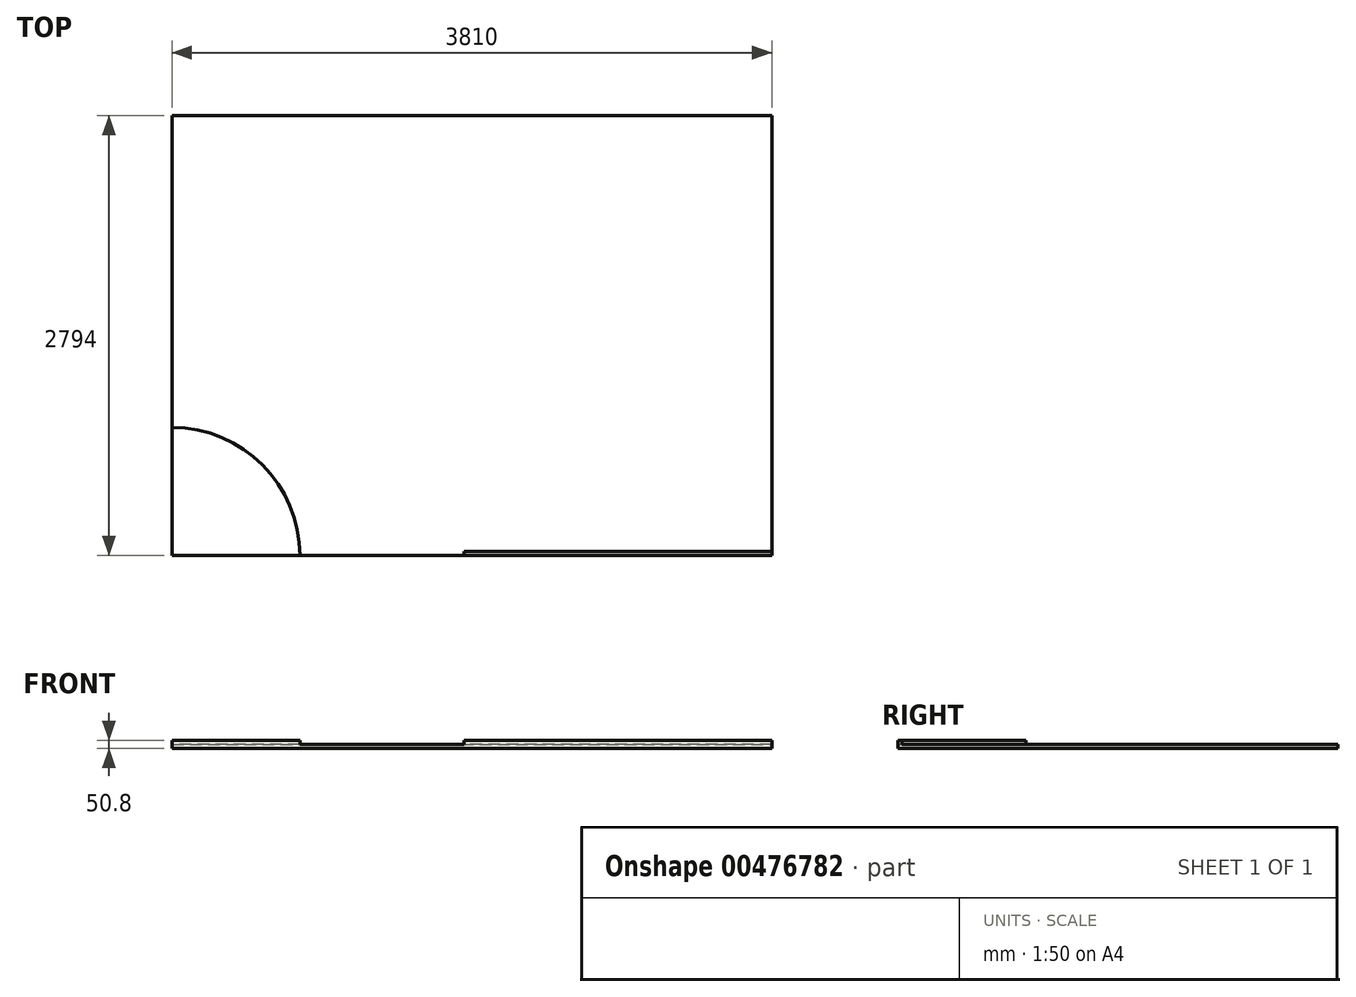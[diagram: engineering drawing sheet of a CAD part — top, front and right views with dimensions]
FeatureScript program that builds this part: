
annotation { "Feature Type Name" : "Feature", "Feature Type Description" : "" }
export const myFeature = defineFeature(function(context is Context, id is Id, definition is map)
    precondition{}
    {
        {
            var Q0;
            Q0=qCreatedBy(makeId("Top.planeOp"),FACE);
            var sketch = newSketch(context, id + "F0", { "sketchPlane" : qUnion([Q0])});
            skLineSegment(sketch, "E0.bottom", {"start": v(0, 0) * mm, "end": v(3810, 0) * mm});
            skLineSegment(sketch, "E0.top", {"start": v(0, 2794) * mm, "end": v(3810, 2794) * mm});
            skLineSegment(sketch, "E0.left", {"start": v(0, 0) * mm, "end": v(0, 2794) * mm});
            skLineSegment(sketch, "E0.right", {"start": v(3810, 0) * mm, "end": v(3810, 2794) * mm});
            skSolve(sketch);
        }
        {
            var Q0;
            Q0 = qSketchRegion(id + "F0", true);
            extrude(context, id + "F1", {"entities" : qUnion([Q0]), "depth" : 25.4 * mm});
        }
        {
            var Q0;
            Q0=makeQuery(id+"F1.opExtrude","CAP_FACE",FACE,{"disambiguationData":[OSD([sQuery(id+"F0.wireOp",EDGE,"E0.bottom"),sQuery(id+"F0.wireOp",EDGE,"E0.top"),sQuery(id+"F0.wireOp",EDGE,"E0.left"),sQuery(id+"F0.wireOp",EDGE,"E0.right")])],"isStart":false});
            var sketch = newSketch(context, id + "F2", { "sketchPlane" : qUnion([Q0])});
            skArc(sketch, "E1", {"start": v(812.8, 0) * mm, "mid": v(574.74, 574.74) * mm, "end": v(0, 812.8) * mm});
            skLineSegment(sketch, "E2.bottom", {"start": v(3810, 0) * mm, "end": v(1854.2, 0) * mm});
            skLineSegment(sketch, "E2.top", {"start": v(3810, 25.4) * mm, "end": v(1854.2, 25.4) * mm});
            skLineSegment(sketch, "E2.left", {"start": v(3810, 0) * mm, "end": v(3810, 25.4) * mm});
            skLineSegment(sketch, "E2.right", {"start": v(1854.2, 0) * mm, "end": v(1854.2, 25.4) * mm});
            skLineSegment(sketch, "E3", {"start": v(0, 812.8) * mm, "end": v(0, 0) * mm});
            skLineSegment(sketch, "E4", {"start": v(812.8, 0) * mm, "end": v(0, 0) * mm});
            skSolve(sketch);
        }
        {
            var Q0;
            Q0 = qSketchRegion(id + "F2", true);
            extrude(context, id + "F3", {"entities" : qUnion([Q0]), "operationType" : NewBodyOperationType.ADD, "depth" : 25.4 * mm, "offsetDistance" : 25.4 * mm});
        }
    });
